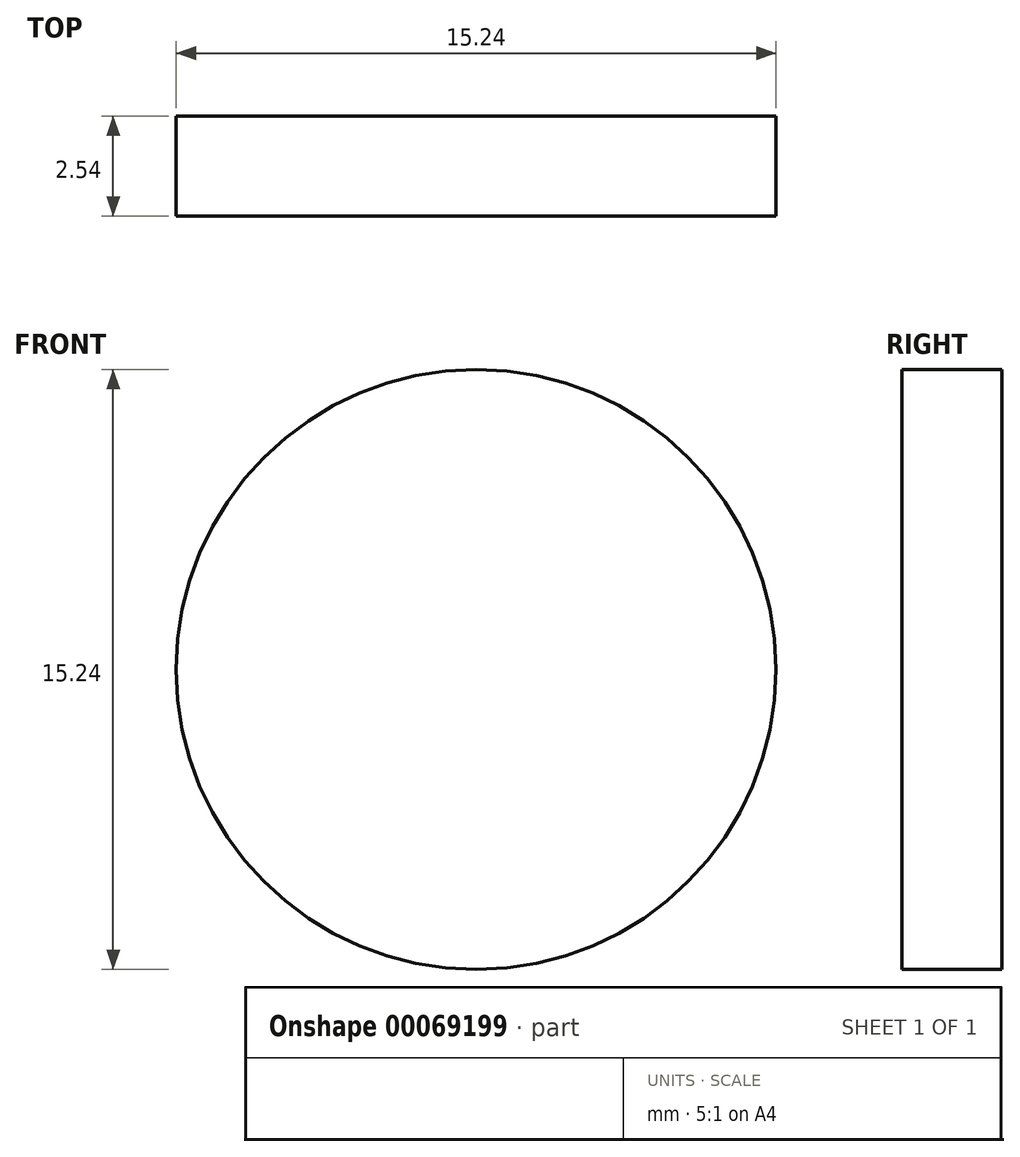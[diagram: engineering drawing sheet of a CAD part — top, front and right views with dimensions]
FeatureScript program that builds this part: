
annotation { "Feature Type Name" : "Feature", "Feature Type Description" : "" }
export const myFeature = defineFeature(function(context is Context, id is Id, definition is map)
    precondition{}
    {
        {
            var Q0;
            Q0=qCreatedBy(makeId("Front.planeOp"),FACE);
            var sketch = newSketch(context, id + "F0", { "sketchPlane" : qUnion([Q0])});
            skCircle(sketch, "E0", {"center": v(0, 0) * mm, "radius": 7.62 * mm});
            skSolve(sketch);
        }
        {
            var Q0;
            Q0 = qSketchRegion(id + "F0", true);
            extrude(context, id + "F1", {"entities" : qUnion([Q0]), "depth" : 2.54 * mm});
        }
    });
